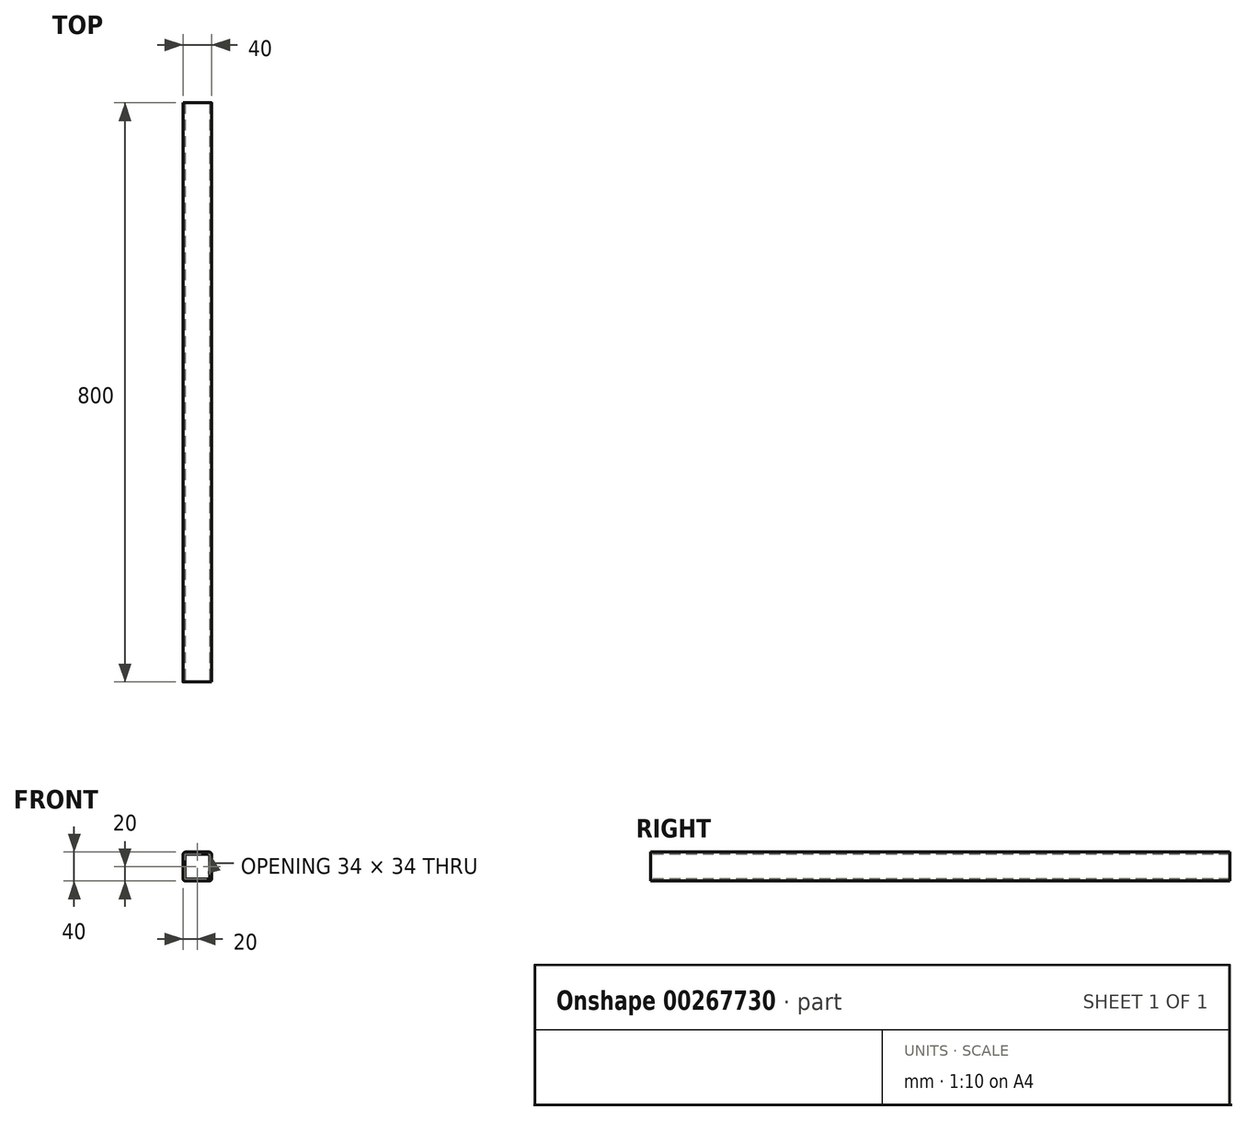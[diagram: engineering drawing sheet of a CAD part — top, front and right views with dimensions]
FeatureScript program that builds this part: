
annotation { "Feature Type Name" : "Feature", "Feature Type Description" : "" }
export const myFeature = defineFeature(function(context is Context, id is Id, definition is map)
    precondition{}
    {
        {
            var Q0;
            Q0=qCreatedBy(makeId("Front.planeOp"),FACE);
            var sketch = newSketch(context, id + "F0", { "sketchPlane" : qUnion([Q0])});
            skLineSegment(sketch, "E0.bottom", {"start": v(16, -20) * mm, "end": v(-16, -20) * mm});
            skLineSegment(sketch, "E0.top", {"start": v(16, 20) * mm, "end": v(-16, 20) * mm});
            skLineSegment(sketch, "E0.left", {"start": v(20, -16) * mm, "end": v(20, 16) * mm});
            skLineSegment(sketch, "E0.right", {"start": v(-20, -16) * mm, "end": v(-20, 16) * mm});
            skPoint(sketch, "E0.middle", {"position": v(0, 0) * mm});
            skPoint(sketch, "E1.visualSharp", {"position": v(-20, 20) * mm});
            skArc(sketch, "E1.filletArc", {"start": v(-16, 20) * mm, "mid": v(-18.83, 18.83) * mm, "end": v(-20, 16) * mm});
            skPoint(sketch, "E2.visualSharp", {"position": v(20, 20) * mm});
            skArc(sketch, "E2.filletArc", {"start": v(20, 16) * mm, "mid": v(18.83, 18.83) * mm, "end": v(16, 20) * mm});
            skPoint(sketch, "E3.visualSharp", {"position": v(20, -20) * mm});
            skArc(sketch, "E3.filletArc", {"start": v(16, -20) * mm, "mid": v(18.83, -18.83) * mm, "end": v(20, -16) * mm});
            skPoint(sketch, "E4.visualSharp", {"position": v(-20, -20) * mm});
            skArc(sketch, "E4.filletArc", {"start": v(-20, -16) * mm, "mid": v(-18.83, -18.83) * mm, "end": v(-16, -20) * mm});
            skArc(sketch, "E5.0", {"start": v(-17, -16) * mm, "mid": v(-16.7, -16.7) * mm, "end": v(-16, -17) * mm});
            skLineSegment(sketch, "E5.1", {"start": v(16, -17) * mm, "end": v(-16, -17) * mm});
            skLineSegment(sketch, "E5.2", {"start": v(-17, -16) * mm, "end": v(-17, 16) * mm});
            skArc(sketch, "E5.3", {"start": v(16, -17) * mm, "mid": v(16.7, -16.7) * mm, "end": v(17, -16) * mm});
            skArc(sketch, "E5.4", {"start": v(-16, 17) * mm, "mid": v(-16.7, 16.7) * mm, "end": v(-17, 16) * mm});
            skLineSegment(sketch, "E5.5", {"start": v(16, 17) * mm, "end": v(-16, 17) * mm});
            skArc(sketch, "E5.6", {"start": v(17, 16) * mm, "mid": v(16.7, 16.7) * mm, "end": v(16, 17) * mm});
            skLineSegment(sketch, "E5.7", {"start": v(17, -16) * mm, "end": v(17, 16) * mm});
            skSolve(sketch);
        }
        {
            var Q0;
            Q0=qSketchRegion(id+"F0",true);
            extrude(context, id + "F1", {"entities" : qUnion([Q0]), "oppositeDirection" : true, "depth" : 800 * mm});
        }
    });
